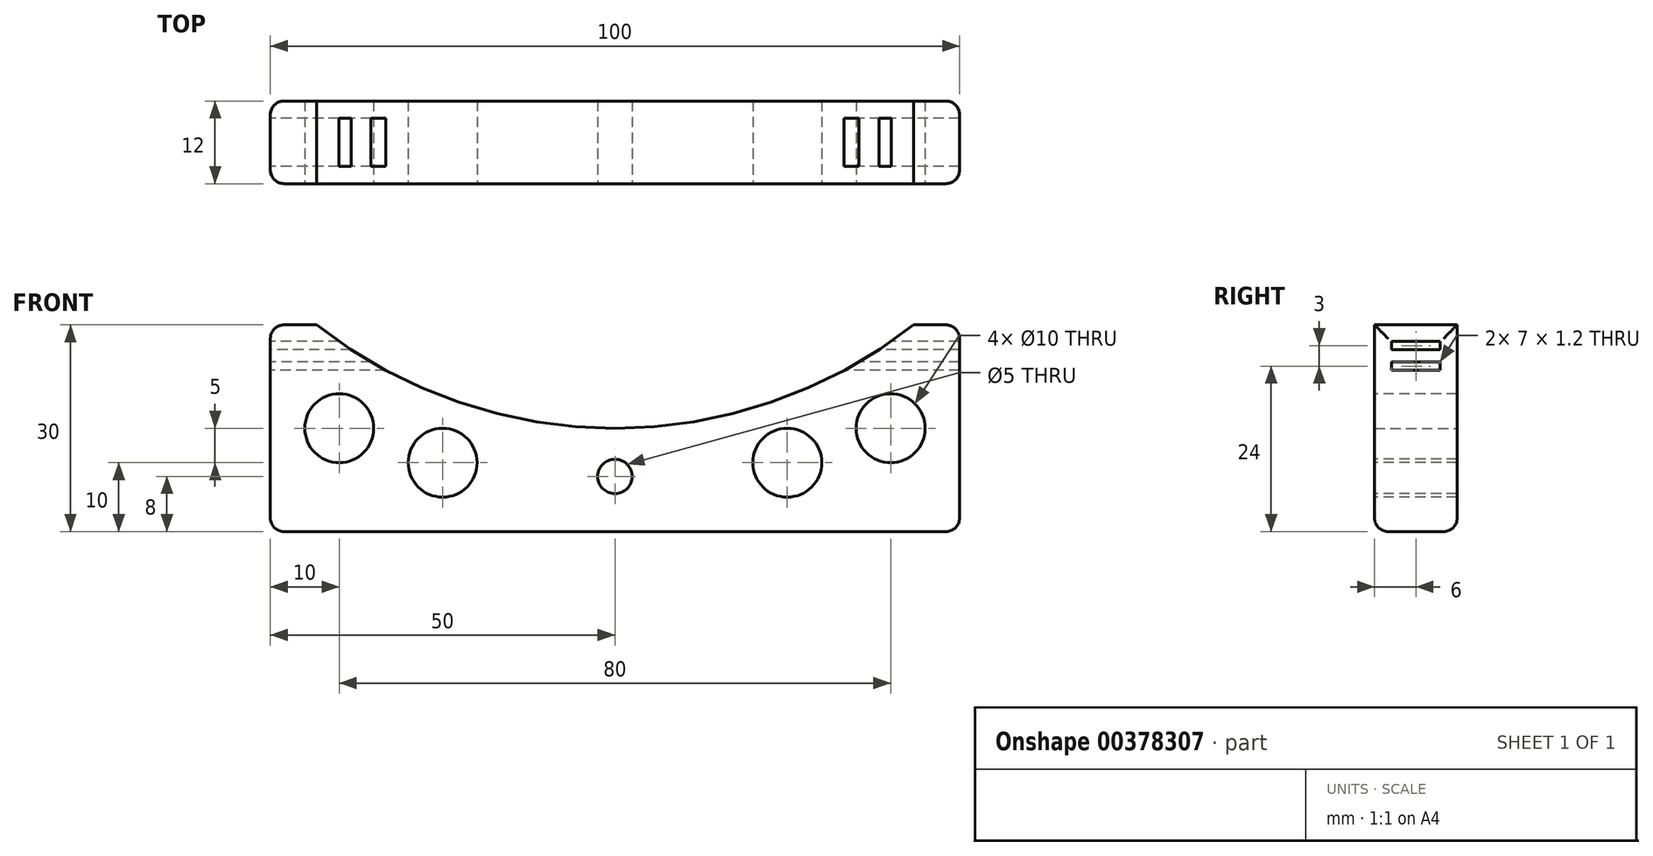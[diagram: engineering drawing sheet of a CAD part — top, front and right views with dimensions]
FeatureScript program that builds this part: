
annotation { "Feature Type Name" : "Feature", "Feature Type Description" : "" }
export const myFeature = defineFeature(function(context is Context, id is Id, definition is map)
    precondition{}
    {
        {
            var Q0;
            Q0=qCreatedBy(makeId("Front.planeOp"),FACE);
            var sketch = newSketch(context, id + "F0", { "sketchPlane" : qUnion([Q0])});
            skLineSegment(sketch, "E0.bottom", {"start": v(50, -15) * mm, "end": v(-50, -15) * mm});
            skLineSegment(sketch, "E0.top", {"start": v(50, 15) * mm, "end": v(-50, 15) * mm});
            skLineSegment(sketch, "E0.left", {"start": v(50, -15) * mm, "end": v(50, 15) * mm});
            skLineSegment(sketch, "E0.right", {"start": v(-50, -15) * mm, "end": v(-50, 15) * mm});
            skPoint(sketch, "E0.middle", {"position": v(0, 0) * mm});
            skLineSegment(sketch, "E1", {"start": v(0, 0) * mm, "end": v(0, 70) * mm});
            skCircle(sketch, "E2", {"center": v(0, 70) * mm, "radius": 70 * mm});
            skSolve(sketch);
        }
        {
            var Q0;
            Q0=makeQuery(id+"F0.imprint","IMPRINT",FACE,{"disambiguationData":[TD([[makeQuery(id+"F0.imprint","IMPRINT",EDGE,{"derivedFrom":sQuery(id+"F0.wireOp",EDGE,"E0.bottom")}),-1.0]])]});
            extrude(context, id + "F1", {"entities" : qUnion([Q0]), "depth" : 12 * mm});
        }
        {
            var Q0;
            Q0=makeQuery(id+"F1.opExtrude","CAP_EDGE",EDGE,{"disambiguationData":[OSD([sQuery(id+"F0.wireOp",EDGE,"E0.bottom")])],"isStart":false});
            var Q1;
            Q1=makeQuery(id+"F1.opExtrude","CAP_EDGE",EDGE,{"disambiguationData":[OSD([sQuery(id+"F0.wireOp",EDGE,"E0.right")])],"isStart":false});
            var Q2;
            Q2=makeQuery(id+"F1.opExtrude","CAP_EDGE",EDGE,{"disambiguationData":[OSD([sQuery(id+"F0.wireOp",EDGE,"E0.left")])],"isStart":false});
            var Q3;
            Q3=makeQuery(id+"F1.opExtrude","CAP_EDGE",EDGE,{"disambiguationData":[OSD([sQuery(id+"F0.wireOp",EDGE,"E0.left")])],"isStart":true});
            var Q4;
            Q4=makeQuery(id+"F1.opExtrude","CAP_EDGE",EDGE,{"disambiguationData":[OSD([sQuery(id+"F0.wireOp",EDGE,"E0.bottom")])],"isStart":true});
            var Q5;
            Q5=makeQuery(id+"F1.opExtrude","CAP_EDGE",EDGE,{"disambiguationData":[OSD([sQuery(id+"F0.wireOp",EDGE,"E0.right")])],"isStart":true});
            var Q6;
            Q6=makeQuery(id+"F1.opExtrude","SWEPT_EDGE",EDGE,{"disambiguationData":[OSD([sQuery(id+"F0.wireOp",EDGE,"E0.bottom"),sQuery(id+"F0.wireOp",EDGE,"E0.right")])]});
            var Q7;
            Q7=makeQuery(id+"F1.opExtrude","SWEPT_EDGE",EDGE,{"disambiguationData":[OSD([sQuery(id+"F0.wireOp",EDGE,"E0.bottom"),sQuery(id+"F0.wireOp",EDGE,"E0.left")])]});
            var Q8;
            Q8=makeQuery(id+"F1.opExtrude","SWEPT_EDGE",EDGE,{"disambiguationData":[OSD([sQuery(id+"F0.wireOp",EDGE,"E0.top"),sQuery(id+"F0.wireOp",EDGE,"E0.left")])]});
            var Q9;
            Q9=makeQuery(id+"F1.opExtrude","SWEPT_EDGE",EDGE,{"disambiguationData":[OSD([sQuery(id+"F0.wireOp",EDGE,"E0.top"),sQuery(id+"F0.wireOp",EDGE,"E0.right")])]});
            fillet(context, id + "F2", {"entities" : qUnion([Q0, Q1, Q2, Q3, Q4, Q5, Q6, Q7, Q8, Q9]), "radius" : 2 * mm, "tangentPropagation" : true, "allowEdgeOverflow" : false});
        }
        {
            var Q0;
            Q0=makeQuery(id+"F1.opExtrude","CAP_FACE",FACE,{"disambiguationData":[OSD([sQuery(id+"F0.wireOp",EDGE,"E0.bottom"),sQuery(id+"F0.wireOp",EDGE,"E0.top"),sQuery(id+"F0.wireOp",EDGE,"E0.left"),sQuery(id+"F0.wireOp",EDGE,"E0.right"),sQuery(id+"F0.wireOp",EDGE,"E2")])],"isStart":false});
            var sketch = newSketch(context, id + "F3", { "sketchPlane" : qUnion([Q0])});
            skPoint(sketch, "E3", {"position": v(-40, 0) * mm});
            skPoint(sketch, "E3.positionSnap0", {"position": v(0, 0) * mm});
            skPoint(sketch, "E4", {"position": v(40, 0) * mm});
            skPoint(sketch, "E5", {"position": v(0, -7) * mm});
            skPoint(sketch, "E6", {"position": v(0, -5) * mm});
            skPoint(sketch, "E7", {"position": v(-25, -5) * mm});
            skPoint(sketch, "E8", {"position": v(25, -5) * mm});
            skCircle(sketch, "E9", {"center": v(-25, -5) * mm, "radius": 5 * mm});
            skCircle(sketch, "E10", {"center": v(0, -7) * mm, "radius": 2.5 * mm});
            skCircle(sketch, "E11", {"center": v(25, -5) * mm, "radius": 5 * mm});
            skCircle(sketch, "E12", {"center": v(-40, 0) * mm, "radius": 5 * mm});
            skCircle(sketch, "E13", {"center": v(40, 0) * mm, "radius": 5 * mm});
            skSolve(sketch);
        }
        {
            var Q0;
            Q0=makeQuery(id+"F3.imprint","IMPRINT",FACE,{"disambiguationData":[TD([[makeQuery(id+"F3.imprint","IMPRINT",EDGE,{"derivedFrom":sQuery(id+"F3.wireOp",EDGE,"E9")}),1.0]])]});
            var Q1;
            Q1=makeQuery(id+"F3.imprint","IMPRINT",FACE,{"disambiguationData":[TD([[makeQuery(id+"F3.imprint","IMPRINT",EDGE,{"derivedFrom":sQuery(id+"F3.wireOp",EDGE,"E12")}),1.0]])]});
            var Q2;
            Q2=makeQuery(id+"F3.imprint","IMPRINT",FACE,{"disambiguationData":[TD([[makeQuery(id+"F3.imprint","IMPRINT",EDGE,{"derivedFrom":sQuery(id+"F3.wireOp",EDGE,"E10")}),1.0]])]});
            var Q3;
            Q3=makeQuery(id+"F3.imprint","IMPRINT",FACE,{"disambiguationData":[TD([[makeQuery(id+"F3.imprint","IMPRINT",EDGE,{"derivedFrom":sQuery(id+"F3.wireOp",EDGE,"E11")}),1.0]])]});
            var Q4;
            Q4=makeQuery(id+"F3.imprint","IMPRINT",FACE,{"disambiguationData":[TD([[makeQuery(id+"F3.imprint","IMPRINT",EDGE,{"derivedFrom":sQuery(id+"F3.wireOp",EDGE,"E13")}),1.0]])]});
            extrude(context, id + "F4", {"entities" : qUnion([Q0, Q1, Q2, Q3, Q4]), "operationType" : NewBodyOperationType.REMOVE, "endBound" : BoundingType.THROUGH_ALL, "oppositeDirection" : true, "depth" : 25 * mm});
        }
        {
            var Q0;
            Q0=makeQuery(id+"F1.opExtrude","SWEPT_FACE",FACE,{"disambiguationData":[OSD([sQuery(id+"F0.wireOp",EDGE,"E0.right")])]});
            var sketch = newSketch(context, id + "F5", { "sketchPlane" : qUnion([Q0])});
            skPoint(sketch, "E14", {"position": v(6, 12) * mm});
            skPoint(sketch, "E15", {"position": v(6, 9) * mm});
            skLineSegment(sketch, "E16.bottom", {"start": v(9.5, 11.4) * mm, "end": v(2.5, 11.4) * mm});
            skLineSegment(sketch, "E16.top", {"start": v(9.5, 12.6) * mm, "end": v(2.5, 12.6) * mm});
            skLineSegment(sketch, "E16.left", {"start": v(9.5, 11.4) * mm, "end": v(9.5, 12.6) * mm});
            skLineSegment(sketch, "E16.right", {"start": v(2.5, 11.4) * mm, "end": v(2.5, 12.6) * mm});
            skLineSegment(sketch, "E17.bottom", {"start": v(9.5, 8.4) * mm, "end": v(2.5, 8.4) * mm});
            skLineSegment(sketch, "E17.top", {"start": v(9.5, 9.6) * mm, "end": v(2.5, 9.6) * mm});
            skLineSegment(sketch, "E17.left", {"start": v(9.5, 8.4) * mm, "end": v(9.5, 9.6) * mm});
            skLineSegment(sketch, "E17.right", {"start": v(2.5, 8.4) * mm, "end": v(2.5, 9.6) * mm});
            skSolve(sketch);
        }
        {
            var Q0;
            Q0=makeQuery(id+"F5.imprint","IMPRINT",FACE,{"disambiguationData":[TD([[makeQuery(id+"F5.imprint","IMPRINT",EDGE,{"derivedFrom":sQuery(id+"F5.wireOp",EDGE,"E16.bottom")}),-1.0]])]});
            var Q1;
            Q1=makeQuery(id+"F5.imprint","IMPRINT",FACE,{"disambiguationData":[TD([[makeQuery(id+"F5.imprint","IMPRINT",EDGE,{"derivedFrom":sQuery(id+"F5.wireOp",EDGE,"E17.bottom")}),-1.0]])]});
            extrude(context, id + "F6", {"entities" : qUnion([Q0, Q1]), "operationType" : NewBodyOperationType.REMOVE, "endBound" : BoundingType.THROUGH_ALL, "oppositeDirection" : true, "depth" : 25 * mm});
        }
    });
